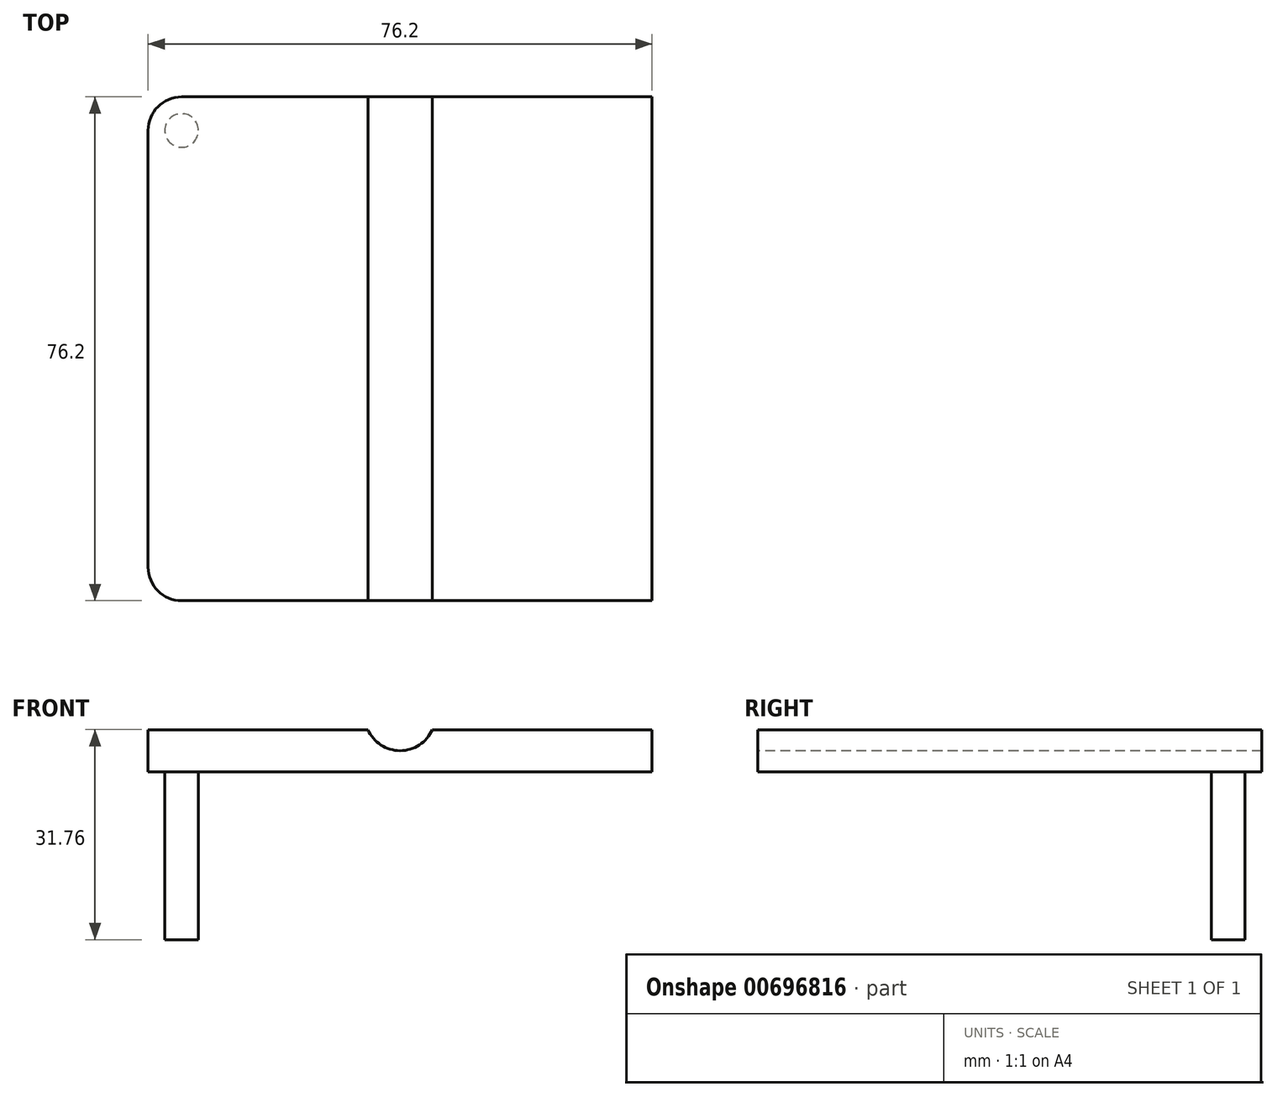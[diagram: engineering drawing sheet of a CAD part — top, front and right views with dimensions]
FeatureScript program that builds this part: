
annotation { "Feature Type Name" : "Feature", "Feature Type Description" : "" }
export const myFeature = defineFeature(function(context is Context, id is Id, definition is map)
    precondition{}
    {
        {
            var Q0;
            Q0=qCreatedBy(makeId("Top.planeOp"),FACE);
            var sketch = newSketch(context, id + "F0", { "sketchPlane" : qUnion([Q0])});
            skLineSegment(sketch, "E0.bottom", {"start": v(38.1, -38.1) * mm, "end": v(-38.1, -38.1) * mm});
            skLineSegment(sketch, "E0.top", {"start": v(38.1, 38.1) * mm, "end": v(-38.1, 38.1) * mm});
            skLineSegment(sketch, "E0.left", {"start": v(38.1, -38.1) * mm, "end": v(38.1, 38.1) * mm});
            skLineSegment(sketch, "E0.right", {"start": v(-38.1, -38.1) * mm, "end": v(-38.1, 38.1) * mm});
            skPoint(sketch, "E0.middle", {"position": v(0, 0) * mm});
            skSolve(sketch);
        }
        {
            var Q0;
            Q0=makeQuery(id+"F0.imprint","IMPRINT",FACE,{"disambiguationData":[TD([[makeQuery(id+"F0.imprint","IMPRINT",EDGE,{"derivedFrom":sQuery(id+"F0.wireOp",EDGE,"E0.bottom")}),-1.0]])]});
            extrude(context, id + "F1", {"entities" : qUnion([Q0]), "endBound" : BoundingType.SYMMETRIC, "depth" : 6.35 * mm, "offsetDistance" : 25.4 * mm});
        }
        {
            var Q0;
            Q0=makeQuery(id+"F1.opExtrude","SWEPT_EDGE",EDGE,{"disambiguationData":[OSD([sQuery(id+"F0.wireOp",EDGE,"E0.top"),sQuery(id+"F0.wireOp",EDGE,"E0.right")])]});
            var Q1;
            Q1=makeQuery(id+"F1.opExtrude","SWEPT_EDGE",EDGE,{"disambiguationData":[OSD([sQuery(id+"F0.wireOp",EDGE,"E0.bottom"),sQuery(id+"F0.wireOp",EDGE,"E0.right")])]});
            fillet(context, id + "F2", {"entities" : qUnion([Q0, Q1]), "radius" : 5.08 * mm, "tangentPropagation" : true, "allowEdgeOverflow" : false});
        }
        {
            var Q0;
            Q0=makeQuery(id+"F1.opExtrude","SWEPT_FACE",FACE,{"disambiguationData":[OSD([sQuery(id+"F0.wireOp",EDGE,"E0.bottom")])]});
            var sketch = newSketch(context, id + "F3", { "sketchPlane" : qUnion([Q0])});
            skArc(sketch, "E1", {"start": v(-4.87, 3.17) * mm, "mid": v(0, 0) * mm, "end": v(4.88, 3.18) * mm});
            skSolve(sketch);
        }
        {
            var Q0;
            {var subQ0=sQuery(id+"F3.wireOp",EDGE,"E1");Q0=makeQuery(id+"F3.imprint","IMPRINT",FACE,{"disambiguationData":[TD([[makeQuery(id+"F3.imprint","IMPRINT",EDGE,{"derivedFrom":subQ0}),1.0]])]});}
            extrude(context, id + "F4", {"entities" : qUnion([Q0]), "operationType" : NewBodyOperationType.REMOVE, "endBound" : BoundingType.THROUGH_ALL, "oppositeDirection" : true, "depth" : 76.2 * mm, "offsetDistance" : 25.4 * mm});
        }
        {
            var Q0;
            Q0=makeQuery(id+"F1.opExtrude","CAP_FACE",FACE,{"disambiguationData":[OSD([sQuery(id+"F0.wireOp",EDGE,"E0.bottom"),sQuery(id+"F0.wireOp",EDGE,"E0.top"),sQuery(id+"F0.wireOp",EDGE,"E0.left"),sQuery(id+"F0.wireOp",EDGE,"E0.right")])],"isStart":true});
            var sketch = newSketch(context, id + "F5", { "sketchPlane" : qUnion([Q0])});
            skCircle(sketch, "E2", {"center": v(-33.02, -33.02) * mm, "radius": 2.54 * mm});
            skSolve(sketch);
        }
        {
            var Q0;
            Q0 = qSketchRegion(id + "F5", true);
            extrude(context, id + "F6", {"entities" : qUnion([Q0]), "operationType" : NewBodyOperationType.ADD, "depth" : 25.4 * mm, "offsetDistance" : 25.4 * mm});
        }
    });
